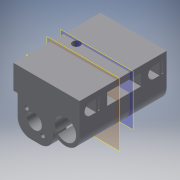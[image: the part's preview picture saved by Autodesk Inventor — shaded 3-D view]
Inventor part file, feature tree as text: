
AUTODESK INVENTOR PART (.ipt)
format: ipt  version: 2016 (Build 200138000, 138)  size: 1,510,912 bytes
history: native  units: mm
features: sketch x7, projected_geometry x5, extrude x4, other x3, hole x2, plane x2, direct_edit x1, move_body x1
ambient origin geometry x8: Origin, YZ Plane, XZ Plane, XY Plane, X Axis, Y Axis, Z Axis, Center Point
bodies: Solid1 (feature_tree)
feature tree (25):
  other  "z_right_printer_1"
  other  "MeshFeature1"
  direct_edit  "Direct Edit1"
  sketch  "Sketch1"  dims[d0=0.0mm d1=0.0mm d2=5.5mm]
  other  "Work Point1"
  hole  "Hole1"  [1 undecoded]
  extrude  "Extrusion1"  Depth=16.0mm
  hole  "Hole2"  [1 undecoded]
  sketch  "Sketch5"  dims[d14=3.2mm d15=6.0mm d16=4.0mm d17=2.0mm d18=90.0deg d19=23.5mm d20=20.594885mm d21=1.0mm]
  extrude  "Extrusion2"  Depth=1.0mm TaperAngle=0.0deg
  extrude  "Extrusion3"  [1 undecoded]
  plane  "Work Plane1"
  plane  "Work Plane2"
  extrude  "Extrusion4"  [1 undecoded]
  projected_geometry  "Projected Loop1"
  sketch  "Sketch3"  dims[d3=10.5mm d4=6.0mm d5=4.0mm d6=2.0mm d7=90.0deg d8=8.0mm d9=20.594885mm d10=16.0mm]
  projected_geometry  "Projected Loop3"
  sketch  "Sketch4"  dims[d11=10.0mm d12=0.0mm d13=16.0mm]
  sketch  "Sketch6"  dims[d22=1.0mm d23=0.0mm d24=1.0mm d25=0.0mm]
  sketch  "Sketch7"  dims[d26=-26.0mm d27=-26.0mm]
  projected_geometry  "Projected Loop5"
  projected_geometry  "Projected Loop6"
  sketch  "Sketch8"  dims[d28=7.5mm d29=0.0mm]
  projected_geometry  "Projected Loop7"
  move_body  "Move1"
note: 4 required parameter values undecoded (feature->parameter linkage not recoverable at this tier; creation-order binding heuristic only, values carry confidence <= 0.55)
